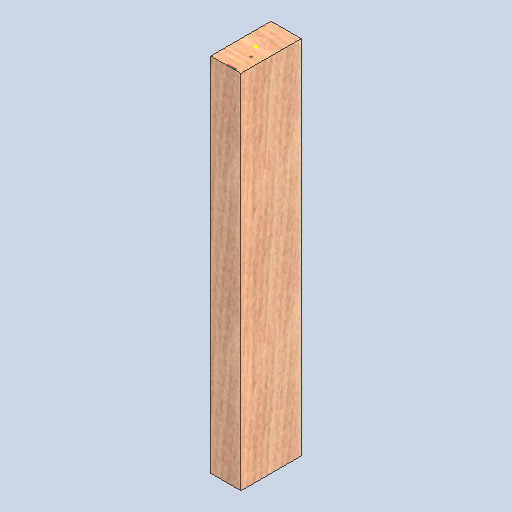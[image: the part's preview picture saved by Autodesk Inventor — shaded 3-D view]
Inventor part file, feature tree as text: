
AUTODESK INVENTOR PART (.ipt)
format: ipt  version: 2025 (Build 290162000, 162)  size: 183,808 bytes
history: native  units: in
note: dims shown in document units (in); Inventor stores cm internally (conversion verified against a paired STEP export)
features: other x3, sketch x2
ambient origin geometry x8: Origin, YZ Plane, XZ Plane, XY Plane, X Axis, Y Axis, Z Axis, Center Point
bodies: Solid1 (feature_tree)
feature tree (5):
  other  "2x4x24.ipt"
  other  "Solid1::2x4x24.ipt"
  other  "TaggingFeature1"
  sketch  "Sketch1"  dims[d0=0.3937in]
  sketch  "Sketch2"
